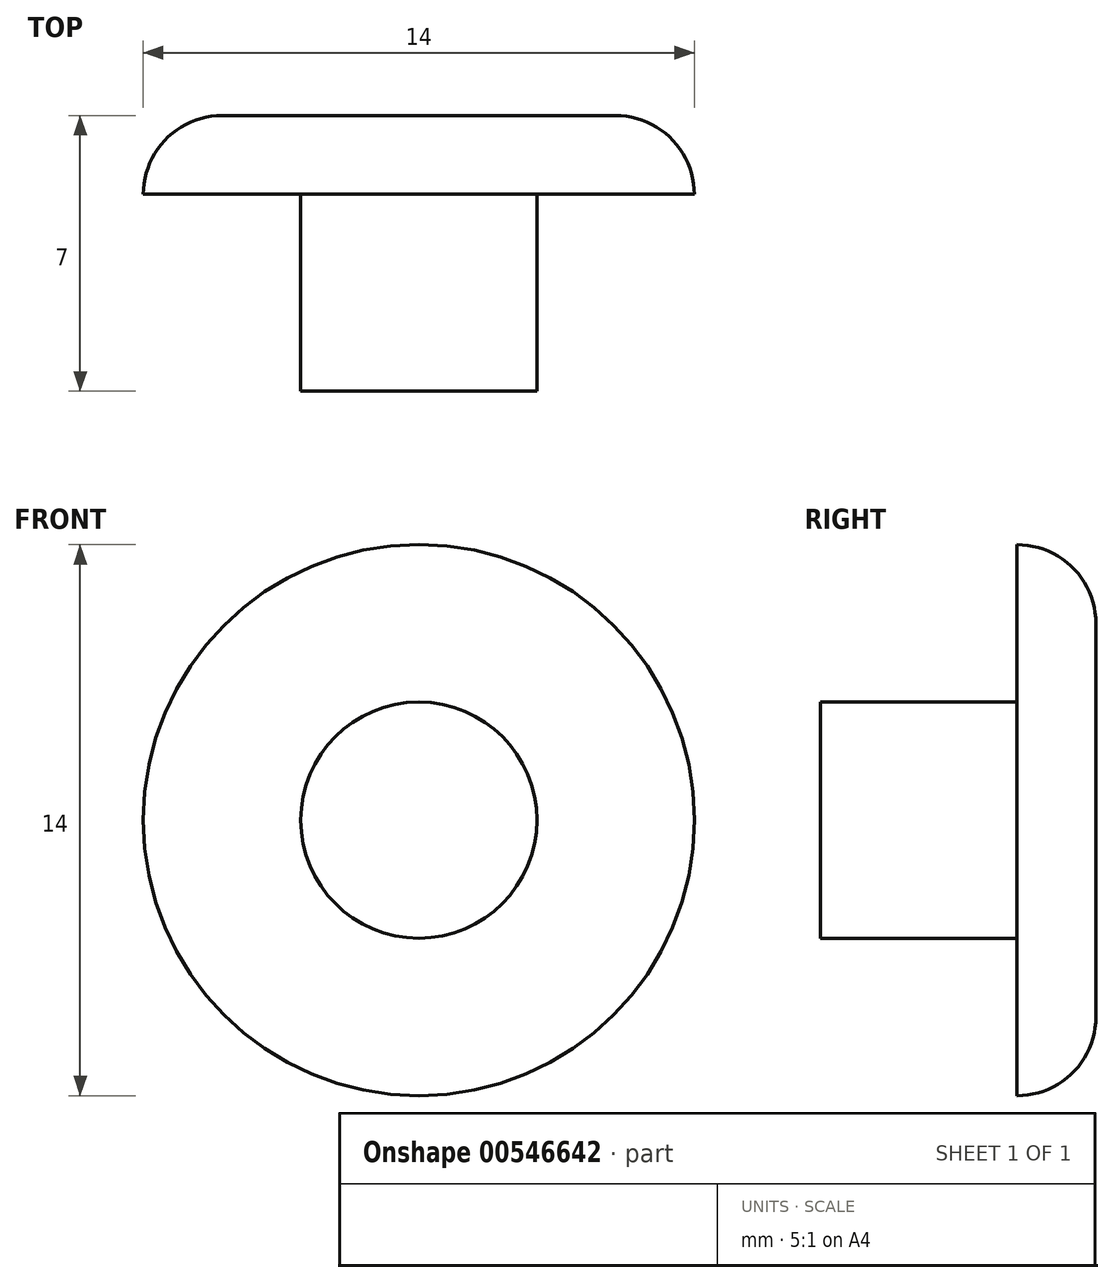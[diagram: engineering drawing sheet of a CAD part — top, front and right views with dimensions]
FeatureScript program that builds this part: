
annotation { "Feature Type Name" : "Feature", "Feature Type Description" : "" }
export const myFeature = defineFeature(function(context is Context, id is Id, definition is map)
    precondition{}
    {
        {
            var Q0;
            Q0=qCreatedBy(makeId("Front.planeOp"),FACE);
            var sketch = newSketch(context, id + "F0", { "sketchPlane" : qUnion([Q0])});
            skCircle(sketch, "E0", {"center": v(0, 0) * mm, "radius": 3 * mm});
            skCircle(sketch, "E1", {"center": v(0, 0) * mm, "radius": 7 * mm});
            skSolve(sketch);
        }
        {
            var Q0;
            Q0=makeQuery(id+"F0.imprint","IMPRINT",FACE,{"disambiguationData":[TD([[makeQuery(id+"F0.imprint","IMPRINT",EDGE,{"derivedFrom":sQuery(id+"F0.wireOp",EDGE,"E0")}),1.0]])]});
            extrude(context, id + "F1", {"entities" : qUnion([Q0]), "depth" : 5 * mm, "offsetDistance" : 25 * mm});
        }
        {
            var Q0;
            Q0=makeQuery(id+"F0.imprint","IMPRINT",FACE,{"disambiguationData":[TD([[makeQuery(id+"F0.imprint","IMPRINT",EDGE,{"derivedFrom":sQuery(id+"F0.wireOp",EDGE,"E0")}),-1.0]])]});
            var Q1;
            Q1=makeQuery(id+"F0.imprint","IMPRINT",FACE,{"disambiguationData":[TD([[makeQuery(id+"F0.imprint","IMPRINT",EDGE,{"derivedFrom":sQuery(id+"F0.wireOp",EDGE,"E0")}),1.0]])]});
            extrude(context, id + "F2", {"entities" : qUnion([Q0, Q1]), "operationType" : NewBodyOperationType.ADD, "oppositeDirection" : true, "depth" : 2 * mm, "offsetDistance" : 25 * mm});
        }
        {
            var Q0;
            Q0=makeQuery(id+"F2.opExtrude","CAP_EDGE",EDGE,{"disambiguationData":[OSD([sQuery(id+"F0.wireOp",EDGE,"E1")])],"isStart":false});
            fillet(context, id + "F3", {"entities" : qUnion([Q0]), "radius" : 2 * mm, "tangentPropagation" : true, "allowEdgeOverflow" : false});
        }
    });
